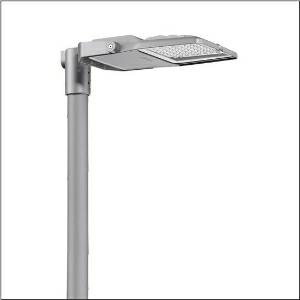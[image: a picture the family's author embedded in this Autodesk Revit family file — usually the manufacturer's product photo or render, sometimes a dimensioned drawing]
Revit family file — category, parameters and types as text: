
# Revit family: floodlight_fl_21_mini___pl64_5xa7771d2e3a_8ccc
name_source: partatom
category: Lighting Fixtures
units: mm (PartAtom-declared; Revit-internal decimal feet)

## family parameters
Cut with Voids When Loaded = No
Host = Face
Light Source = No
Part Type = Normal
Room Calculation Point = No
Round Connector Dimension = Use Diameter
Shared = No

## types (1)
- --- (1 x LED, 17220 lm, 143 W, 3000K)
    Apparent Load = 143 VA
    CIE Flux Codes = 28 80 98 100 100
    Color Rendering = 70
    Color Temperature = 3000K
    Default Elevation = 1800 mm
    Description = Floodlight FL 21 mini, floodlight, primary light control with lens, of PMMA, primary optical cover: protective disc, of toughened safety glass, transparent, light distribution: PL64, light emission: direct distribution, installation type: surface-mounted, LED, High Power LED, rated luminous flux: 17.220lm, luminous efficacy: 120lm/W, light colour: 730, colour temperature: 3000K, control gear: ECG iQ, control: Auto-Match, Temp-Guard, Lumen-Switch, Night-Set, Smart-Wire, Light-Fading, Desk-Remote (wireless, voltage-free reading and setting of iQ features in the workshop via application-optimized NFC function/RFID function), optimised constant luminous flux control (CLO 2.0), with terminal, 6-pole, mains connection: 220..240V, AC, 50/60Hz, start of lifetime: 143W, end of lifetime: 152W, reduction: 61W, luminaire housing, of diecast aluminium, powder-coated, Siteco® metallic grey (DB 702S), corrosivity category C5 according to DIN EN ISO 12944, mast bracket, of steel, galvanised, powder-coated, Siteco® metallic grey (DB 702S), protection rating (complete): IP66, insulation class (complete): insulation class II (safety insulation), certification: CE, ENEC, VDE, protection symbol: D, impact resistance: IK08, permissible operating ambient temperature: -40..+40°C, permissible operating ambient temperature for outdoor applications: -40..+50°C, standard: DIN EN 12944, packaging unit: 1 piece

Light Distribution: PL64
    Height = 70 mm
    Lamp = 1 x LED
    Lamp Light Flux = 17220 lm
    Lamp Power = 143 W
    Lamp count = 1
    Length = 485 mm
    Luminous efficacy = 120 lm/W
    Manufacturer = Siteco
    ModVariant = No
    Model = 5XA7771D2E3A
    Number of Poles = 1
    OnlyDefault = Yes
    Power Factor = 1
    Product Name = Floodlight FL 21 mini | PL64
    Product group = floodlight | pylon top
    ProductGroupID = 6101
    Protection Class = Protection class II
    Protection Degree = IP 66
    RLX_Detail_Level = 1
    RlxData = <blob elided: 101385 chars, md5=0423db2b>
    Socket = socket
    Standby Power = 0 W
    System Light Flux = 17220 lm
    System Power = 143 W
    Type Comments = factory setting: luminous flux: 100 % | dim-lin: 254 | 730 mA
    Type Image = l_1007125.jpg
    URL = http://relux.com
    VarID = @adj_077119
    Voltage = 0 V
    Weight = 0.00 kg
    Width = 337 mm

## geometry (parser evidence)
native form markers: Blend x4, Sweep x13
no freeform markers — native parametric forms only
